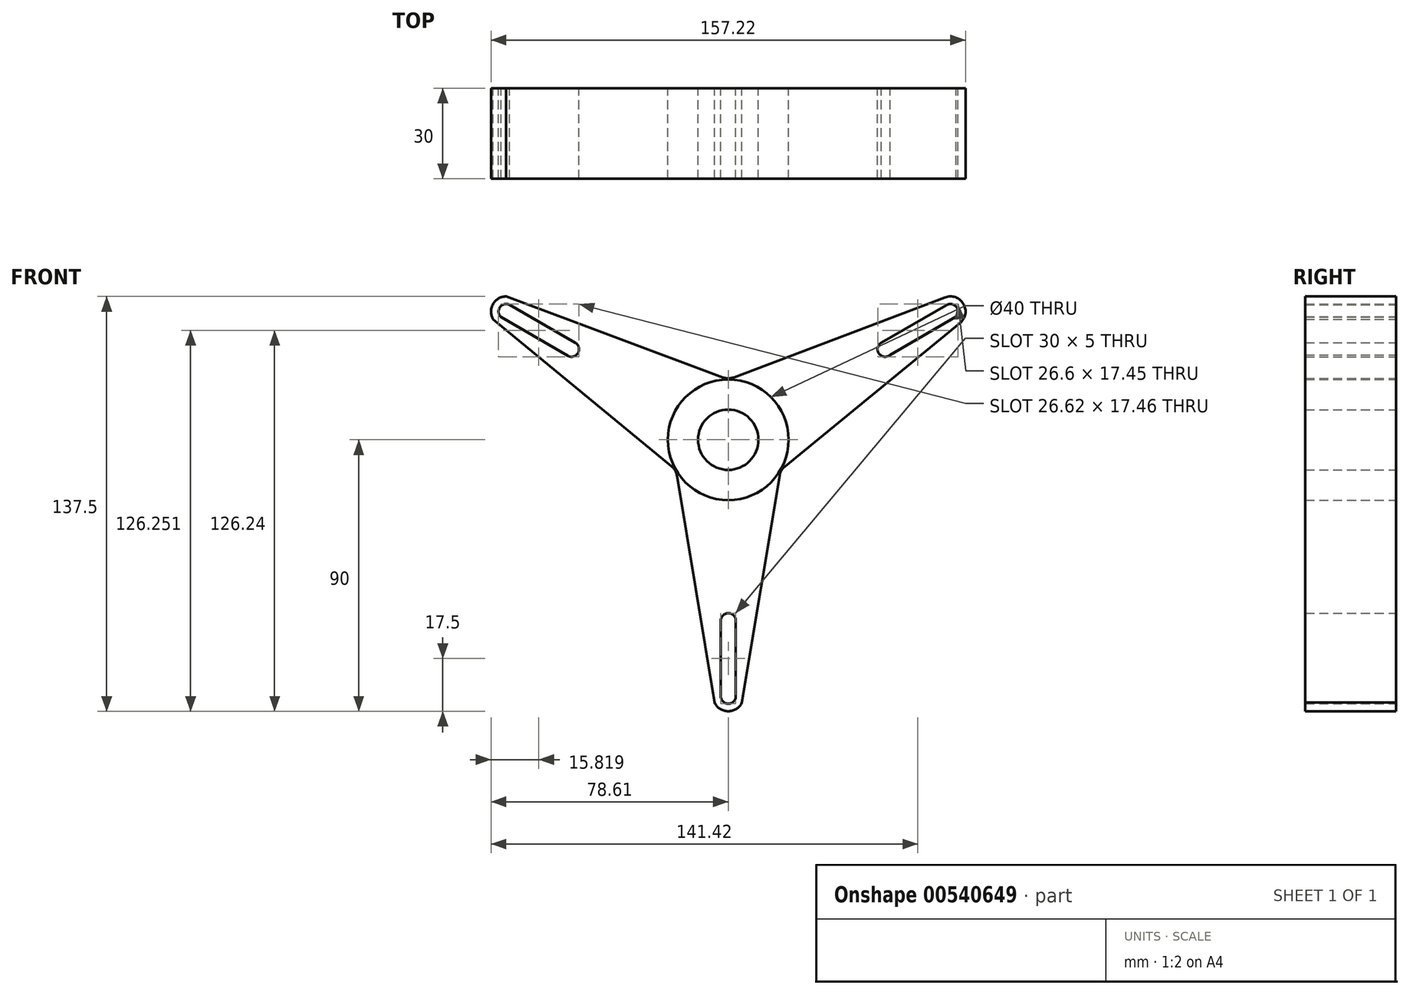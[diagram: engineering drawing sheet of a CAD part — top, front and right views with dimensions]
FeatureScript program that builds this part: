
annotation { "Feature Type Name" : "Feature", "Feature Type Description" : "" }
export const myFeature = defineFeature(function(context is Context, id is Id, definition is map)
    precondition{}
    {
        {
            var Q0;
            Q0=qCreatedBy(makeId("Front.planeOp"),FACE);
            var sketch = newSketch(context, id + "F0", { "sketchPlane" : qUnion([Q0])});
            skCircle(sketch, "E0", {"center": v(0, 0) * mm, "radius": 10 * mm});
            skCircle(sketch, "E1", {"center": v(0, 0) * mm, "radius": 20 * mm});
            skArc(sketch, "E2", {"start": v(-4.52, -87.14) * mm, "mid": v(0, -90) * mm, "end": v(4.52, -87.14) * mm});
            skLineSegment(sketch, "E3", {"start": v(-4.52, -87.14) * mm, "end": v(-17.01, -11.85) * mm});
            skLineSegment(sketch, "E4", {"start": v(4.52, -87.14) * mm, "end": v(17.01, -11.86) * mm});
            skArc(sketch, "E5", {"start": v(-2.5, -85) * mm, "mid": v(0, -87.5) * mm, "end": v(2.5, -85) * mm});
            skArc(sketch, "E6", {"start": v(2.5, -60) * mm, "mid": v(0, -57.5) * mm, "end": v(-2.5, -60) * mm});
            skLineSegment(sketch, "E7", {"start": v(-2.5, -60) * mm, "end": v(-2.5, -85) * mm});
            skLineSegment(sketch, "E8", {"start": v(2.5, -60) * mm, "end": v(2.5, -85) * mm});
            skArc(sketch, "E9", {"start": v(-73.65, 47.5) * mm, "mid": v(-77.97, 44.95) * mm, "end": v(-77.9, 39.92) * mm});
            skLineSegment(sketch, "E10", {"start": v(-73.65, 47.5) * mm, "end": v(-1.76, 20.66) * mm});
            skLineSegment(sketch, "E11", {"start": v(-77.9, 39.92) * mm, "end": v(-18.77, -8.8) * mm});
            skArc(sketch, "E12", {"start": v(-72.45, 44.71) * mm, "mid": v(-75.65, 43.95) * mm, "end": v(-75.32, 40.67) * mm});
            skCircle(sketch, "E13", {"center": v(-51.96, 30) * mm, "radius": 2.5 * mm});
            skLineSegment(sketch, "E14", {"start": v(-75.32, 40.67) * mm, "end": v(-53.22, 27.84) * mm});
            skLineSegment(sketch, "E15", {"start": v(-72.45, 44.71) * mm, "end": v(-50.71, 32.17) * mm});
            skArc(sketch, "E16", {"start": v(76.78, 38.63) * mm, "mid": v(77.94, 45) * mm, "end": v(71.84, 47.18) * mm});
            skLineSegment(sketch, "E17", {"start": v(1.76, 20.66) * mm, "end": v(71.84, 47.18) * mm});
            skLineSegment(sketch, "E18", {"start": v(18.78, -8.8) * mm, "end": v(76.78, 38.63) * mm});
            skArc(sketch, "E19", {"start": v(75.43, 40.78) * mm, "mid": v(75.57, 44.05) * mm, "end": v(72.36, 44.67) * mm});
            skArc(sketch, "E20", {"start": v(50.75, 32.19) * mm, "mid": v(49.93, 28.55) * mm, "end": v(53.64, 28.14) * mm});
            skLineSegment(sketch, "E21", {"start": v(50.67, 32.14) * mm, "end": v(72.36, 44.67) * mm});
            skLineSegment(sketch, "E22", {"start": v(52.74, 27.62) * mm, "end": v(75.43, 40.78) * mm});
            skPoint(sketch, "E23.visualSharp", {"position": v(0, 20) * mm});
            skArc(sketch, "E23.filletArc", {"start": v(-1.76, 20.66) * mm, "mid": v(0, 20.34) * mm, "end": v(1.76, 20.66) * mm});
            skPoint(sketch, "E24.visualSharp", {"position": v(-17.32, -10) * mm});
            skArc(sketch, "E24.filletArc", {"start": v(-17.01, -11.85) * mm, "mid": v(-17.61, -10.17) * mm, "end": v(-18.77, -8.8) * mm});
            skPoint(sketch, "E25.visualSharp", {"position": v(17.32, -10) * mm});
            skArc(sketch, "E25.filletArc", {"start": v(18.78, -8.8) * mm, "mid": v(17.62, -10.17) * mm, "end": v(17.01, -11.86) * mm});
            skSolve(sketch);
        }
        {
            var Q0;
            Q0 = qSketchRegion(id + "F0", true);
            var Q1;
            Q1=makeQuery(id+"F0.imprint","IMPRINT",FACE,{"disambiguationData":[TD([[makeQuery(id+"F0.imprint","IMPRINT",EDGE,{"derivedFrom":sQuery(id+"F0.wireOp",EDGE,"E1")}),-1.0]])]});
            var Q2;
            Q2=makeQuery(id+"F0.imprint","IMPRINT",FACE,{"disambiguationData":[TD([[makeQuery(id+"F0.imprint","IMPRINT",EDGE,{"derivedFrom":sQuery(id+"F0.wireOp",EDGE,"E0")}),1.0]])]});
            extrude(context, id + "F1", {"entities" : qUnion([Q0, Q1, Q2]), "depth" : 30 * mm, "offsetDistance" : 25 * mm});
        }
    });
